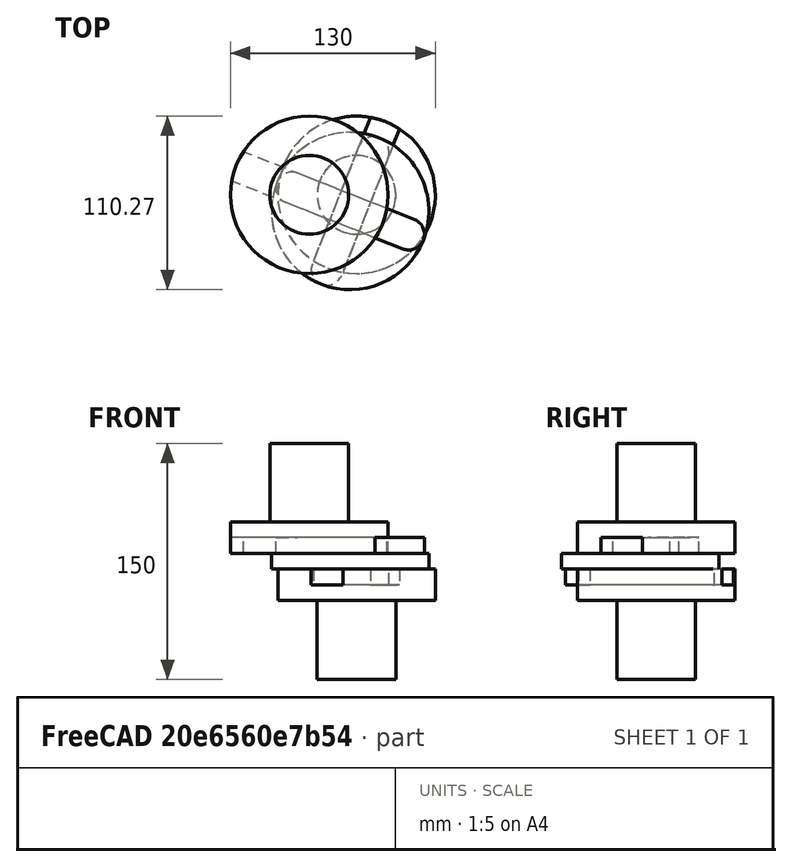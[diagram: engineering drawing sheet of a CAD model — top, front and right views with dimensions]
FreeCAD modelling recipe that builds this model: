
FCSTD DOCUMENT  (FreeCAD 0.18R14555 (Git shallow))
Label: ACOPLAMENTO
License: All rights reserved
LicenseURL: http://en.wikipedia.org/wiki/All_rights_reserved
objects: Part::Cylinder×4, App::DocumentObjectGroupPython×4, Part::Feature×3, Part::MultiFuse×3, Part::Box×1, Part::Fillet×1, Part::Cut×1
note: 13 computed .brp shape members not serialized (recipe doc carries the construction recipe); baked Part::Feature solids carry a one-line shape summary decoded from their .brp

FEATURE [Part::Box] Box  label="Cube"
  AttacherType = Attacher::AttachEngine3D
  Height = 10
  Length = 100
  Placement = pos=(-50,-10,-10) rot=(0,0,1;0rad)
  Width = 20
FEATURE [Part::Cylinder] Cylinder
  Angle = 360
  AttacherType = Attacher::AttachEngine3D
  Height = 10
  Radius = 50
FEATURE [Part::Fillet] Fillet
  Base = -> Box
  Edges = 4 edges r=9.99: [Edge1,Edge3,Edge5,Edge7]
FEATURE [Part::Feature] Fillet001
  Placement = pos=(0,0,20) rot=(0,0,-1;1.5708rad)
  shape: bbox 20 x 100 x 10 mm, 10 faces (baked)
FEATURE [Part::MultiFuse] Fusion  label="CENTRO"
  Placement = pos=(10.9345,-10.2682,0) rot=(0,0,1;4.3354rad)
  Shapes = -> [Cylinder,Fillet,Fillet001]
FEATURE [Part::Cylinder] Cylinder001
  Angle = 360
  AttacherType = Attacher::AttachEngine3D
  Height = 20
  Placement = pos=(0,0,10) rot=(0,0,1;0rad)
  Radius = 50
FEATURE [Part::Cylinder] Cylinder002
  Angle = 360
  AttacherType = Attacher::AttachEngine3D
  Height = 50
  Placement = pos=(0,0,30) rot=(0,0,1;0rad)
  Radius = 25
FEATURE [Part::Feature] Box001  label="Cube001"
  Placement = pos=(-10,50,10) rot=(0,0,-1;1.5708rad)
  shape: bbox 20 x 100 x 10 mm, 6 faces (baked)
FEATURE [Part::MultiFuse] Fusion001
  Shapes = -> [Cylinder001,Cylinder002]
FEATURE [Part::Cut] Cut  label="SUPERIOR"
  Base = -> Fusion001
  Placement = pos=(-15,0,0) rot=(0,0,1;4.3354rad)
  Tool = -> Box001
FEATURE [Part::Feature] Cut001
  Placement = pos=(-1e-15,0,10) rot=(0.707107,-0.707107,0;3.14159rad)
  shape: bbox 100 x 100 x 70 mm, 9 faces (baked)
FEATURE [Part::Cylinder] Cylinder003
  Angle = 360
  AttacherType = Attacher::AttachEngine3D
  Height = 1
  Placement = pos=(0,0,-20) rot=(0,0,1;0rad)
  Radius = 25
FEATURE [Part::MultiFuse] Fusion002  label="INFERIOR"
  Placement = pos=(15,0,0) rot=(0,0,1;4.3354rad)
  Shapes = -> [Cylinder003,Cut001]
FEATURE [App::DocumentObjectGroupPython] My_Placer  # scripted group (container) (typed FeaturePython)
  Placement = pos=(10.9345,-10.2682,0) rot=(0,0,1;60.8841rad)
  RotAxis = (0,0,1)
  RotCenter = (0,0,0)
  arc = time*360
  arc0 = 0
  arc1 = 90
  target = -> Fusion
  time = 9.69
  x = -15*x0
  x0 = -0.728969
  x1 = 200
  y = -15*y0
  y0 = 0.684547
  y1 = 0
  z = 0
  z0 = 0
  z1 = 0
  expr: y0 = sin(time * 720)
  expr: x0 = cos(time * 720)
FEATURE [App::DocumentObjectGroupPython] My_Placer001  # scripted group (container) (typed FeaturePython)
  Placement = pos=(-15,0,0) rot=(0,0,1;60.8841rad)
  RotAxis = (0,0,1)
  RotCenter = (0,0,0)
  arc = time*360
  arc0 = 0
  arc1 = 90
  target = -> Cut
  time = 9.69
  x = -15
  x0 = 0
  x1 = 200
  y = 0
  y0 = 0
  y1 = 0
  z = 0
  z0 = 0
  z1 = 0
FEATURE [App::DocumentObjectGroupPython] My_Placer002  # scripted group (container) (typed FeaturePython)
  Placement = pos=(15,0,0) rot=(0,0,1;60.8841rad)
  RotAxis = (0,0,1)
  RotCenter = (0,0,0)
  arc = time*360
  arc0 = 0
  arc1 = 90
  target = -> Fusion002
  time = 9.69
  x = 15
  x0 = 0
  x1 = 200
  y = 0
  y0 = 0
  y1 = 0
  z = 0
  z0 = 0
  z1 = 0
FEATURE [App::DocumentObjectGroupPython] My_Manager  # scripted group (container) (typed FeaturePython)
  Group = -> [My_Placer,My_Placer001,My_Placer002]
  intervall = 1000
  sleeptime = 0.02
  start = 0
  step = 970
  text = NO
